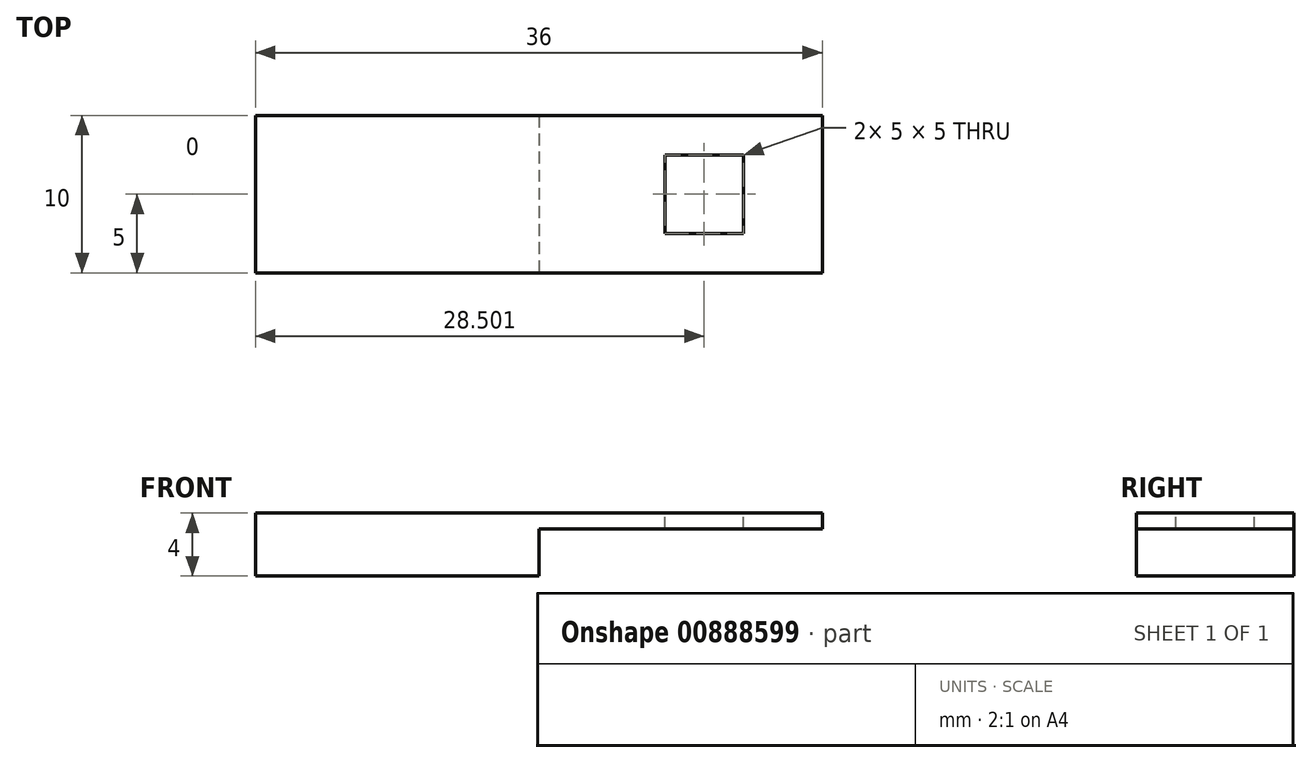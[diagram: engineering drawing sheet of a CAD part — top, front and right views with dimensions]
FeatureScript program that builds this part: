
annotation { "Feature Type Name" : "Feature", "Feature Type Description" : "" }
export const myFeature = defineFeature(function(context is Context, id is Id, definition is map)
    precondition{}
    {
        {
            var Q0;
            Q0=qCreatedBy(makeId("Front.planeOp"),FACE);
            var sketch = newSketch(context, id + "F0", { "sketchPlane" : qUnion([Q0])});
            skLineSegment(sketch, "E0", {"start": v(8.26, 0) * mm, "end": v(16.52, 0) * mm});
            skLineSegment(sketch, "E1", {"start": v(18, 4) * mm, "end": v(44.26, 4) * mm});
            skLineSegment(sketch, "E2", {"start": v(44.26, 4) * mm, "end": v(44.26, 3) * mm});
            skLineSegment(sketch, "E3", {"start": v(44.26, 3) * mm, "end": v(26.26, 3) * mm});
            skLineSegment(sketch, "E4", {"start": v(26.26, 3) * mm, "end": v(26.26, 0) * mm});
            skLineSegment(sketch, "E5", {"start": v(18, 4) * mm, "end": v(8.26, 4) * mm});
            skLineSegment(sketch, "E6", {"start": v(26.26, 0) * mm, "end": v(8.26, 0) * mm});
            skLineSegment(sketch, "E7", {"start": v(8.26, 0) * mm, "end": v(8.26, 4) * mm});
            skPoint(sketch, "E8.end.orphan", {"position": v(0, 0) * mm});
            skPoint(sketch, "E9.orphan", {"position": v(0, 4) * mm});
            skSolve(sketch);
        }
        {
            var Q0;
            Q0=makeQuery(id+"F0.imprint","IMPRINT",FACE,{"disambiguationData":[TD([[makeQuery(id+"F0.imprint","IMPRINT",EDGE,{"derivedFrom":sQuery(id+"F0.wireOp",EDGE,"E1")}),-1.0]])]});
            extrude(context, id + "F1", {"entities" : qUnion([Q0]), "oppositeDirection" : true, "depth" : 10 * mm, "offsetDistance" : 25 * mm});
        }
        {
            var Q0;
            Q0=makeQuery(id+"F1.opExtrude","SWEPT_FACE",FACE,{"disambiguationData":[OSD([sQuery(id+"F0.wireOp",EDGE,"E1"),sQuery(id+"F0.wireOp",EDGE,"E5")])]});
            var sketch = newSketch(context, id + "F2", { "sketchPlane" : qUnion([Q0])});
            skLineSegment(sketch, "E10", {"start": v(25.53, -2.72) * mm, "end": v(25.53, -3.51) * mm});
            skLineSegment(sketch, "E11", {"start": v(25.53, -3.51) * mm, "end": v(39.26, -3.51) * mm});
            skLineSegment(sketch, "E12", {"start": v(39.26, 7.5) * mm, "end": v(39.26, 2.5) * mm});
            skLineSegment(sketch, "E13", {"start": v(39.26, 2.5) * mm, "end": v(34.26, 2.5) * mm});
            skLineSegment(sketch, "E14", {"start": v(34.26, 2.5) * mm, "end": v(34.26, 7.5) * mm});
            skLineSegment(sketch, "E15", {"start": v(34.26, 7.5) * mm, "end": v(39.26, 7.5) * mm});
            skSolve(sketch);
        }
        {
            var Q0;
            Q0=makeQuery(id+"F2.imprint","IMPRINT",FACE,{"disambiguationData":[TD([[makeQuery(id+"F2.imprint","IMPRINT",EDGE,{"derivedFrom":sQuery(id+"F2.wireOp",EDGE,"E12")}),-1.0]])]});
            extrude(context, id + "F3", {"entities" : qUnion([Q0]), "operationType" : NewBodyOperationType.REMOVE, "oppositeDirection" : true, "depth" : 10 * mm, "offsetDistance" : 25 * mm});
        }
    });
